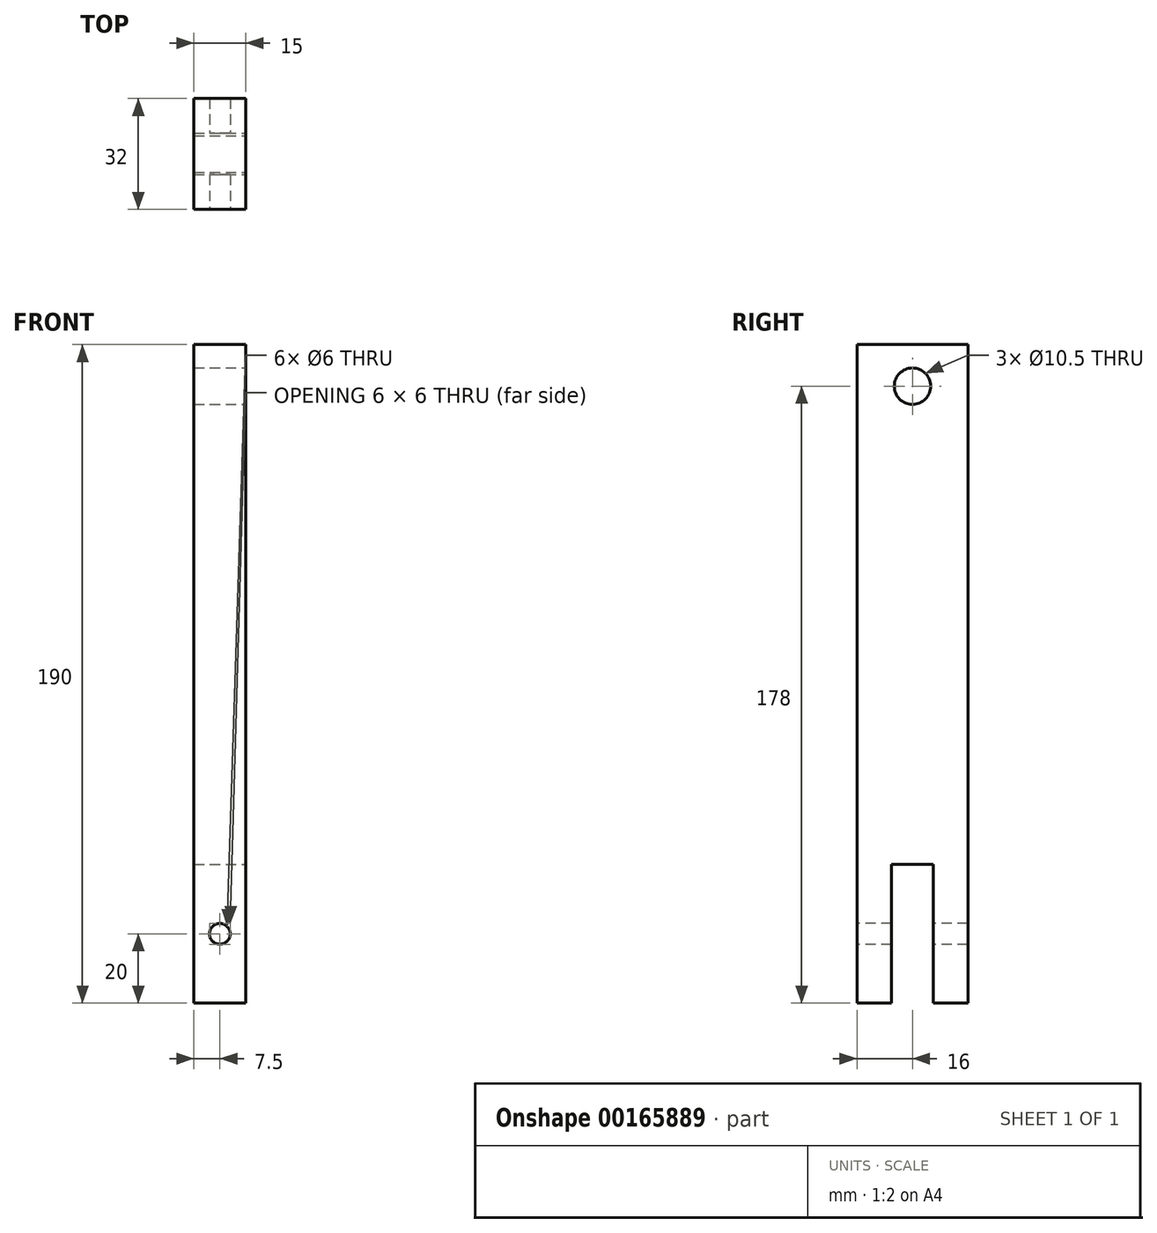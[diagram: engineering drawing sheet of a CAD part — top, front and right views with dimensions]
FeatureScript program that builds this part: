
annotation { "Feature Type Name" : "Feature", "Feature Type Description" : "" }
export const myFeature = defineFeature(function(context is Context, id is Id, definition is map)
    precondition{}
    {
        {
            var Q0;
            Q0=qCreatedBy(makeId("Right.planeOp"),FACE);
            var sketch = newSketch(context, id + "F0", { "sketchPlane" : qUnion([Q0])});
            skLineSegment(sketch, "E0.top", {"start": v(-6, 0) * mm, "end": v(6, 0) * mm});
            skLineSegment(sketch, "E1.bottom", {"start": v(-6, -40) * mm, "end": v(-16, -40) * mm});
            skLineSegment(sketch, "E1.top", {"start": v(16, 150) * mm, "end": v(-16, 150) * mm});
            skLineSegment(sketch, "E1.right", {"start": v(-16, -40) * mm, "end": v(-16, 150) * mm});
            skLineSegment(sketch, "E2.MirrorCS", {"start": v(16, -40) * mm, "end": v(16, 150) * mm});
            skLineSegment(sketch, "E3.MirrorCS", {"start": v(6, -40) * mm, "end": v(16, -40) * mm});
            skLineSegment(sketch, "E4", {"start": v(-6, -40) * mm, "end": v(-6, 0) * mm});
            skLineSegment(sketch, "E5", {"start": v(6, 0) * mm, "end": v(6, -40) * mm});
            skCircle(sketch, "E6", {"center": v(0, 138) * mm, "radius": 5.25 * mm});
            skSolve(sketch);
        }
        {
            var Q0;
            Q0 = qSketchRegion(id + "F0", true);
            extrude(context, id + "F1", {"entities" : qUnion([Q0]), "oppositeDirection" : true, "depth" : 15 * mm});
        }
        {
            var Q0;
            Q0=qCreatedBy(makeId("Front.planeOp"),FACE);
            var sketch = newSketch(context, id + "F2", { "sketchPlane" : qUnion([Q0])});
            skCircle(sketch, "E7", {"center": v(-7.5, -20) * mm, "radius": 3 * mm});
            skPoint(sketch, "E8", {"position": v(-9.95, 0) * mm});
            skPoint(sketch, "E9", {"position": v(-7.5, -40) * mm});
            skSolve(sketch);
        }
        {
            var Q0;
            Q0 = qSketchRegion(id + "F2", true);
            extrude(context, id + "F3", {"entities" : qUnion([Q0]), "operationType" : NewBodyOperationType.REMOVE, "oppositeDirection" : true, "depth" : 25 * mm, "hasSecondDirection" : true, "secondDirectionOppositeDirection" : false, "secondDirectionDepth" : 25 * mm});
        }
    });
